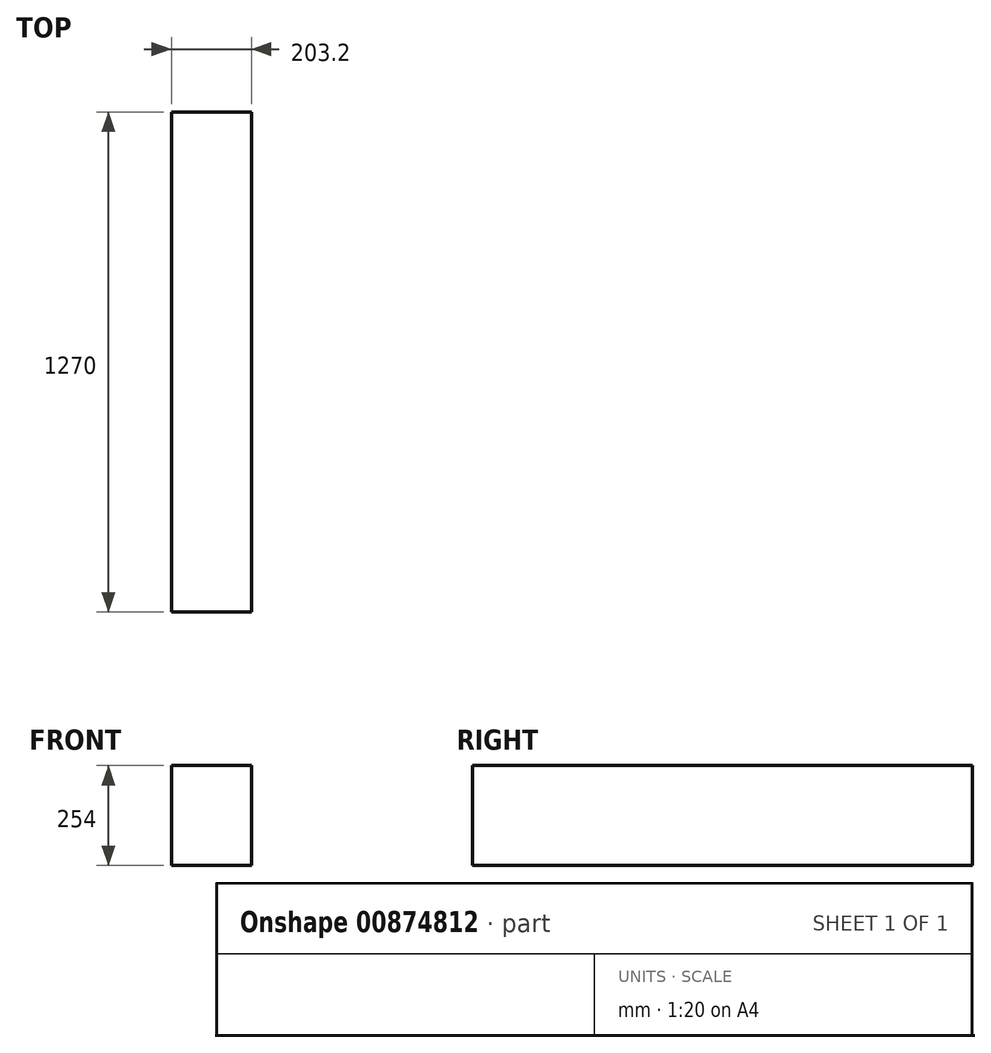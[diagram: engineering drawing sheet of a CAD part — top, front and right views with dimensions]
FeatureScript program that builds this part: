
annotation { "Feature Type Name" : "Feature", "Feature Type Description" : "" }
export const myFeature = defineFeature(function(context is Context, id is Id, definition is map)
    precondition{}
    {
        {
            var Q0;
            Q0=qCreatedBy(makeId("Front.planeOp"),FACE);
            var sketch = newSketch(context, id + "F0", { "sketchPlane" : qUnion([Q0])});
            skLineSegment(sketch, "E0.bottom", {"start": v(-224.47, 221.64) * mm, "end": v(-21.27, 221.64) * mm});
            skLineSegment(sketch, "E0.top", {"start": v(-224.47, -32.36) * mm, "end": v(-21.27, -32.36) * mm});
            skLineSegment(sketch, "E0.left", {"start": v(-224.47, 221.64) * mm, "end": v(-224.47, -32.36) * mm});
            skLineSegment(sketch, "E0.right", {"start": v(-21.27, 221.64) * mm, "end": v(-21.27, -32.36) * mm});
            skSolve(sketch);
        }
        {
            var Q0;
            Q0=makeQuery(id+"F0.imprint","IMPRINT",FACE,{"disambiguationData":[TD([[makeQuery(id+"F0.imprint","IMPRINT",EDGE,{"derivedFrom":sQuery(id+"F0.wireOp",EDGE,"E0.bottom")}),-1.0]])]});
            extrude(context, id + "F1", {"entities" : qUnion([Q0]), "depth" : 1270 * mm, "offsetDistance" : 25.4 * mm});
        }
    });
